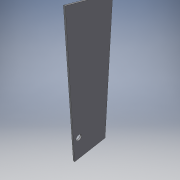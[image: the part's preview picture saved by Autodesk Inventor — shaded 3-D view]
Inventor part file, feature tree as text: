
AUTODESK INVENTOR PART (.ipt)
format: ipt  version: 2016 (Build 200138000, 138)  size: 98,304 bytes
history: native  units: in
note: dims shown in document units (in); Inventor stores cm internally (conversion verified against a paired STEP export)
features: extrude x2, sketch x2
ambient origin geometry x8: Origin, YZ Plane, XZ Plane, XY Plane, X Axis, Y Axis, Z Axis, Center Point
bodies: Solid1 (feature_tree)
feature tree (4):
  extrude  "Extrusion1"  Depth=18.5in
  extrude  "Extrusion2"  Depth=0.75in
  sketch  "Sketch1"  dims[d0=62.0in d1=18.5in]
  sketch  "Sketch2"  dims[d2=0.75in d3=0.0in d5=3.0in d8=2.8in d9=12.0in d12=1.0in d13=0.0in]
